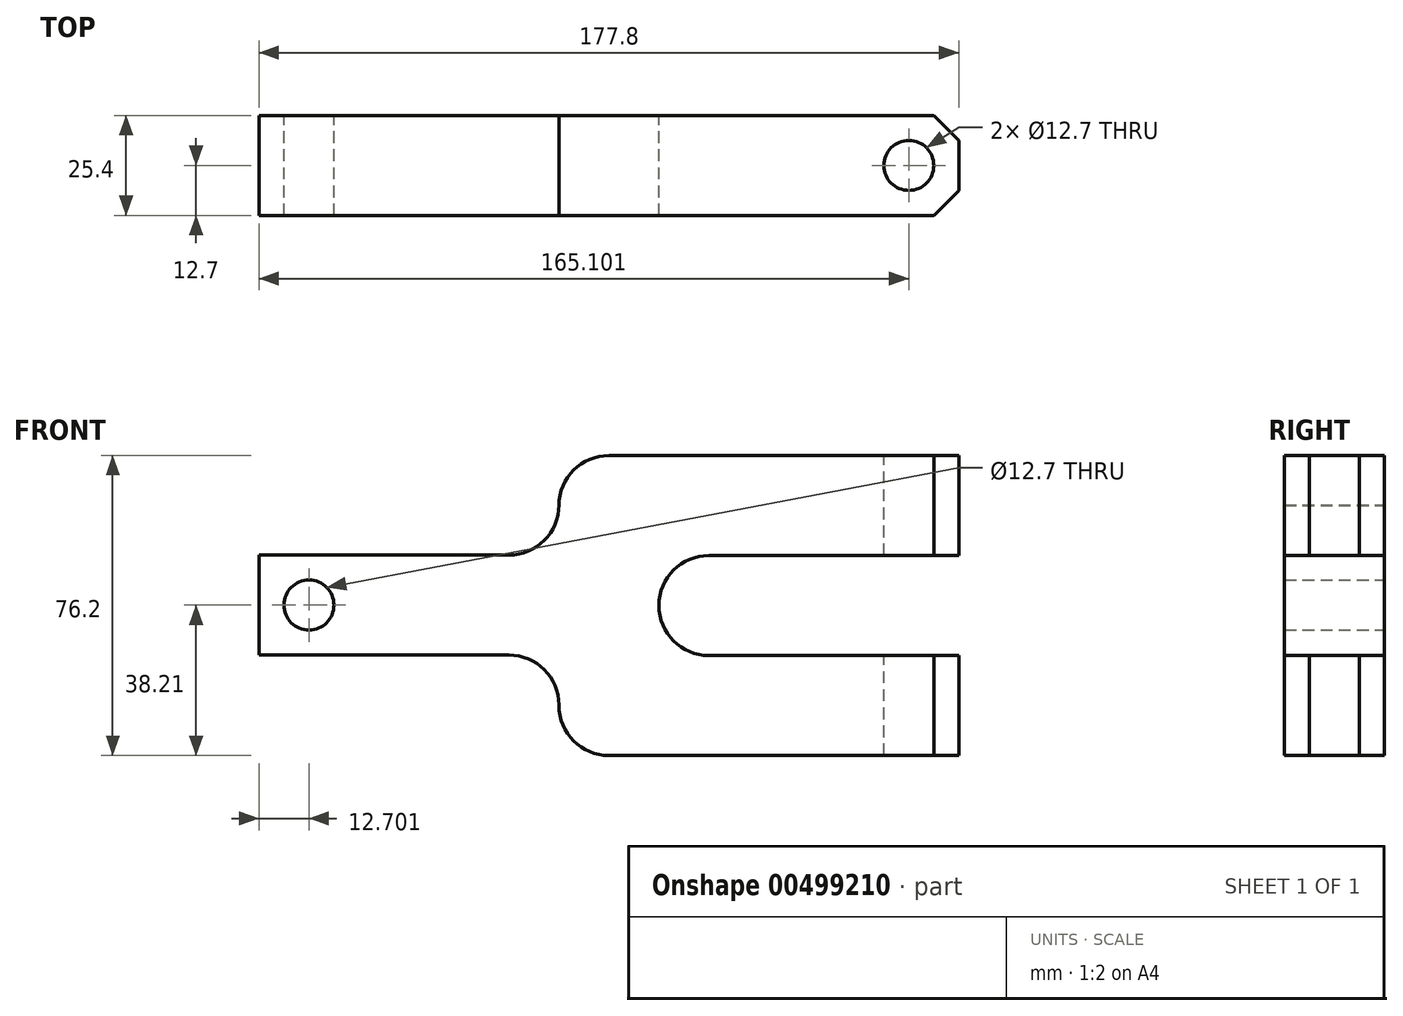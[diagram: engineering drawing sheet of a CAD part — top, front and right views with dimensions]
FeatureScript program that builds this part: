
annotation { "Feature Type Name" : "Feature", "Feature Type Description" : "" }
export const myFeature = defineFeature(function(context is Context, id is Id, definition is map)
    precondition{}
    {
        {
            var Q0;
            Q0=qCreatedBy(makeId("Front.planeOp"),FACE);
            var sketch = newSketch(context, id + "F0", { "sketchPlane" : qUnion([Q0])});
            skLineSegment(sketch, "E0.bottom", {"start": v(-78.2, 12.7) * mm, "end": v(-14.7, 12.7) * mm});
            skLineSegment(sketch, "E0.top", {"start": v(-78.2, -12.7) * mm, "end": v(-14.7, -12.7) * mm});
            skLineSegment(sketch, "E0.left", {"start": v(-78.2, 12.7) * mm, "end": v(-78.2, -12.7) * mm});
            skLineSegment(sketch, "E0.right", {"start": v(23.4, -0.11) * mm, "end": v(23.4, -0.11) * mm});
            skLineSegment(sketch, "E1.bottom", {"start": v(10.7, 37.99) * mm, "end": v(99.6, 37.99) * mm});
            skLineSegment(sketch, "E1.top", {"start": v(36.1, 12.59) * mm, "end": v(99.6, 12.59) * mm});
            skLineSegment(sketch, "E1.left", {"start": v(-2, 25.4) * mm, "end": v(-2, 25.29) * mm});
            skLineSegment(sketch, "E1.right", {"start": v(99.6, 37.99) * mm, "end": v(99.6, 12.59) * mm});
            skLineSegment(sketch, "E2.bottom", {"start": v(36.1, -12.81) * mm, "end": v(99.6, -12.81) * mm});
            skLineSegment(sketch, "E2.top", {"start": v(10.7, -38.21) * mm, "end": v(99.6, -38.21) * mm});
            skLineSegment(sketch, "E2.left", {"start": v(-2, -25.4) * mm, "end": v(-2, -25.51) * mm});
            skLineSegment(sketch, "E2.right", {"start": v(99.6, -12.81) * mm, "end": v(99.6, -38.21) * mm});
            skPoint(sketch, "E3.visualSharp", {"position": v(-2, 37.99) * mm});
            skArc(sketch, "E3.filletArc", {"start": v(10.7, 37.99) * mm, "mid": v(1.71, 34.27) * mm, "end": v(-2, 25.29) * mm});
            skPoint(sketch, "E4.visualSharp", {"position": v(-2, -38.21) * mm});
            skArc(sketch, "E4.filletArc", {"start": v(-2, -25.51) * mm, "mid": v(1.71, -34.5) * mm, "end": v(10.7, -38.21) * mm});
            skPoint(sketch, "E5.newPointB", {"position": v(0, -12.7) * mm});
            skArc(sketch, "E5.filletArc", {"start": v(-2, -25.4) * mm, "mid": v(-5.73, -16.42) * mm, "end": v(-14.7, -12.7) * mm});
            skPoint(sketch, "E6.newPointB", {"position": v(0, 12.7) * mm});
            skArc(sketch, "E6.filletArc", {"start": v(-14.7, 12.7) * mm, "mid": v(-5.73, 16.42) * mm, "end": v(-2, 25.4) * mm});
            skArc(sketch, "E7.filletArc", {"start": v(36.1, 12.59) * mm, "mid": v(27.11, 8.87) * mm, "end": v(23.4, -0.11) * mm});
            skArc(sketch, "E8.filletArc", {"start": v(23.4, -0.11) * mm, "mid": v(27.11, -9.1) * mm, "end": v(36.1, -12.81) * mm});
            skCircle(sketch, "E9", {"center": v(-65.5, 0) * mm, "radius": 6.35 * mm});
            skPoint(sketch, "E10", {"position": v(86.9, -38.21) * mm});
            skSolve(sketch);
        }
        {
            var Q0;
            Q0 = qSketchRegion(id + "F0", true);
            var Q1;
            Q1 = qSketchRegion(id + "F2", true);
            extrude(context, id + "F1", {"entities" : qUnion([Q0, Q1]), "endBound" : BoundingType.SYMMETRIC, "depth" : 25.4 * mm});
        }
        {
            var Q0;
            Q0=qCreatedBy(makeId("Top.planeOp"),FACE);
            var sketch = newSketch(context, id + "F2", { "sketchPlane" : qUnion([Q0])});
            skCircle(sketch, "E11", {"center": v(86.9, 0) * mm, "radius": 6.35 * mm});
            skSolve(sketch);
        }
        {
            var Q0;
            Q0=makeQuery(id+"F2.imprint","IMPRINT",FACE,{"disambiguationData":[TD([[makeQuery(id+"F2.imprint","IMPRINT",EDGE,{"derivedFrom":sQuery(id+"F2.wireOp",EDGE,"E11")}),1.0]])]});
            var Q1;
            Q1=sQuery(id+"F2.wireOp",EDGE,"E11");
            extrude(context, id + "F3", {"entities" : qUnion([Q0]), "operationType" : NewBodyOperationType.REMOVE, "surfaceEntities" : qUnion([Q1]), "endBound" : BoundingType.SYMMETRIC, "oppositeDirection" : true, "depth" : 88.9 * mm});
        }
        {
            var Q0;
            Q0=makeQuery(id+"F1.opExtrude","CAP_EDGE",EDGE,{"disambiguationData":[OSD([sQuery(id+"F0.wireOp",EDGE,"E1.right")])],"isStart":false});
            chamfer(context, id + "F4", {"entities" : qUnion([Q0]), "width" : 6.35 * mm, "tangentPropagation" : true});
        }
        {
            var Q0;
            Q0=makeQuery(id+"F1.opExtrude","CAP_EDGE",EDGE,{"disambiguationData":[OSD([sQuery(id+"F0.wireOp",EDGE,"E1.right")])],"isStart":true});
            chamfer(context, id + "F5", {"entities" : qUnion([Q0]), "width" : 6.35 * mm, "tangentPropagation" : true});
        }
        {
            var Q0;
            Q0=makeQuery(id+"F1.opExtrude","CAP_EDGE",EDGE,{"disambiguationData":[OSD([sQuery(id+"F0.wireOp",EDGE,"E2.right")])],"isStart":false});
            chamfer(context, id + "F6", {"entities" : qUnion([Q0]), "width" : 6.35 * mm, "tangentPropagation" : true});
        }
        {
            var Q0;
            Q0=makeQuery(id+"F1.opExtrude","CAP_EDGE",EDGE,{"disambiguationData":[OSD([sQuery(id+"F0.wireOp",EDGE,"E2.right")])],"isStart":true});
            chamfer(context, id + "F7", {"entities" : qUnion([Q0]), "width" : 6.35 * mm, "tangentPropagation" : true});
        }
    });
